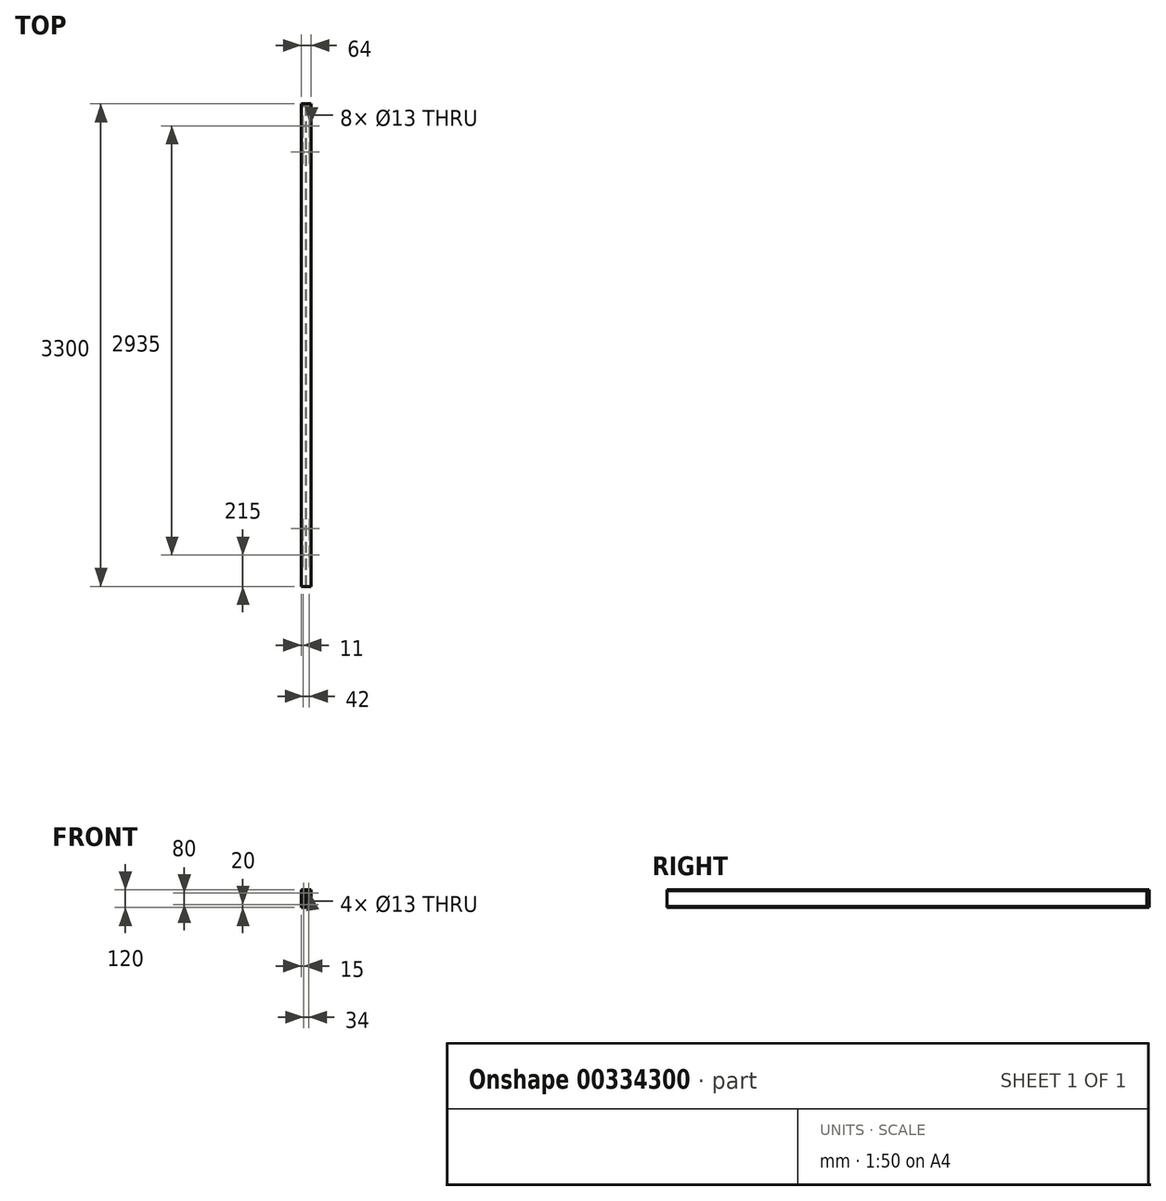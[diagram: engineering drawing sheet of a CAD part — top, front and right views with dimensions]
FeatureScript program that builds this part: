
annotation { "Feature Type Name" : "Feature", "Feature Type Description" : "" }
export const myFeature = defineFeature(function(context is Context, id is Id, definition is map)
    precondition{}
    {
        {
            var Q0;
            Q0=qCreatedBy(makeId("Front.planeOp"),FACE);
            var sketch = newSketch(context, id + "F0", { "sketchPlane" : qUnion([Q0])});
            skLineSegment(sketch, "E0", {"start": v(-32, 0) * mm, "end": v(32, 0) * mm});
            skLineSegment(sketch, "E1", {"start": v(32, 0) * mm, "end": v(32, 6.3) * mm});
            skLineSegment(sketch, "E2", {"start": v(32, 6.3) * mm, "end": v(9.2, 6.3) * mm});
            skLineSegment(sketch, "E3", {"start": v(2.2, 13.3) * mm, "end": v(2.2, 106.7) * mm});
            skLineSegment(sketch, "E4", {"start": v(9.2, 113.7) * mm, "end": v(32, 113.7) * mm});
            skLineSegment(sketch, "E5", {"start": v(32, 113.7) * mm, "end": v(32, 120) * mm});
            skLineSegment(sketch, "E6", {"start": v(32, 120) * mm, "end": v(-32, 120) * mm});
            skLineSegment(sketch, "E7", {"start": v(-32, 120) * mm, "end": v(-32, 113.7) * mm});
            skLineSegment(sketch, "E8", {"start": v(-32, 113.7) * mm, "end": v(-9.2, 113.7) * mm});
            skLineSegment(sketch, "E9", {"start": v(-2.2, 106.7) * mm, "end": v(-2.2, 13.3) * mm});
            skLineSegment(sketch, "E10", {"start": v(-9.2, 6.3) * mm, "end": v(-32, 6.3) * mm});
            skLineSegment(sketch, "E11", {"start": v(-32, 6.3) * mm, "end": v(-32, 0) * mm});
            skLineSegment(sketch, "E12", {"start": v(0, 0) * mm, "end": v(0, 0) * mm});
            skPoint(sketch, "E13.visualSharp", {"position": v(-2.2, 113.7) * mm});
            skArc(sketch, "E13.filletArc", {"start": v(-2.2, 106.7) * mm, "mid": v(-4.25, 111.65) * mm, "end": v(-9.2, 113.7) * mm});
            skPoint(sketch, "E14.visualSharp", {"position": v(-2.2, 6.3) * mm});
            skArc(sketch, "E14.filletArc", {"start": v(-9.2, 6.3) * mm, "mid": v(-4.25, 8.35) * mm, "end": v(-2.2, 13.3) * mm});
            skPoint(sketch, "E15.visualSharp", {"position": v(2.2, 6.3) * mm});
            skArc(sketch, "E15.filletArc", {"start": v(2.2, 13.3) * mm, "mid": v(4.25, 8.35) * mm, "end": v(9.2, 6.3) * mm});
            skPoint(sketch, "E16.visualSharp", {"position": v(2.2, 113.7) * mm});
            skArc(sketch, "E16.filletArc", {"start": v(9.2, 113.7) * mm, "mid": v(4.25, 111.65) * mm, "end": v(2.2, 106.7) * mm});
            skSolve(sketch);
        }
        {
            var Q0;
            Q0=makeQuery(id+"F0.imprint","IMPRINT",FACE,{"disambiguationData":[TD([[makeQuery(id+"F0.imprint","IMPRINT",EDGE,{"derivedFrom":sQuery(id+"F0.wireOp",EDGE,"E0")}),1.0]])]});
            extrude(context, id + "F1", {"entities" : qUnion([Q0]), "depth" : 300 * mm, "hasSecondDirection" : true, "secondDirectionOppositeDirection" : true, "secondDirectionDepth" : 3000 * mm});
        }
        {
            var Q0;
            Q0=makeQuery(id+"F1.opExtrude","CAP_FACE",FACE,{"disambiguationData":[OSD([sQuery(id+"F0.wireOp",EDGE,"E0"),sQuery(id+"F0.wireOp",EDGE,"E1"),sQuery(id+"F0.wireOp",EDGE,"E2"),sQuery(id+"F0.wireOp",EDGE,"E3"),sQuery(id+"F0.wireOp",EDGE,"E4"),sQuery(id+"F0.wireOp",EDGE,"E5"),sQuery(id+"F0.wireOp",EDGE,"E6"),sQuery(id+"F0.wireOp",EDGE,"E7"),sQuery(id+"F0.wireOp",EDGE,"E8"),sQuery(id+"F0.wireOp",EDGE,"E9"),sQuery(id+"F0.wireOp",EDGE,"E10"),sQuery(id+"F0.wireOp",EDGE,"E11"),sQuery(id+"F0.wireOp",EDGE,"E13.filletArc"),sQuery(id+"F0.wireOp",EDGE,"E14.filletArc"),sQuery(id+"F0.wireOp",EDGE,"E15.filletArc"),sQuery(id+"F0.wireOp",EDGE,"E16.filletArc")])],"isStart":true});
            var sketch = newSketch(context, id + "F2", { "sketchPlane" : qUnion([Q0])});
            skLineSegment(sketch, "E17.bottom", {"start": v(-32, 0) * mm, "end": v(32, 0) * mm});
            skLineSegment(sketch, "E17.top", {"start": v(-32, 120) * mm, "end": v(32, 120) * mm});
            skLineSegment(sketch, "E17.left", {"start": v(-32, 0) * mm, "end": v(-32, 120) * mm});
            skLineSegment(sketch, "E17.right", {"start": v(32, 0) * mm, "end": v(32, 120) * mm});
            skCircle(sketch, "E18", {"center": v(-17, 100) * mm, "radius": 6.5 * mm});
            skCircle(sketch, "E19", {"center": v(17, 100) * mm, "radius": 6.5 * mm});
            skCircle(sketch, "E20", {"center": v(17, 20) * mm, "radius": 6.5 * mm});
            skCircle(sketch, "E21", {"center": v(-17, 20) * mm, "radius": 6.5 * mm});
            skLineSegment(sketch, "E22", {"start": v(-17, 100) * mm, "end": v(17, 100) * mm, "construction": true});
            skLineSegment(sketch, "E23", {"start": v(-17, 20) * mm, "end": v(17, 20) * mm, "construction": true});
            skLineSegment(sketch, "E24", {"start": v(0, 120) * mm, "end": v(0, 0) * mm, "construction": true});
            skPoint(sketch, "E24.startSnap0", {"position": v(0, 120) * mm});
            skLineSegment(sketch, "E25", {"start": v(-32, 60) * mm, "end": v(32, 60) * mm, "construction": true});
            skSolve(sketch);
        }
        {
            var Q0;
            Q0=makeQuery(id+"F2.imprint","IMPRINT",FACE,{"disambiguationData":[TD([[makeQuery(id+"F2.imprint","IMPRINT",EDGE,{"derivedFrom":sQuery(id+"F2.wireOp",EDGE,"E19")}),-1.0]])]});
            var Q1;
            Q1=makeQuery(id+"F2.imprint","IMPRINT",FACE,{"disambiguationData":[TD([[makeQuery(id+"F2.imprint","IMPRINT",EDGE,{"derivedFrom":sQuery(id+"F2.wireOp",EDGE,"E18")}),-1.0]])]});
            var Q2;
            {var subQ3=sQuery(id+"F2.wireOp",EDGE,"E17.bottom");Q2=makeQuery(id+"F2.imprint","IMPRINT",FACE,{"disambiguationData":[TD([[makeQuery(id+"F2.imprint","IMPRINT",EDGE,{"derivedFrom":subQ3}),-1.0]])]});}
            extrude(context, id + "F3", {"entities" : qUnion([Q0, Q1, Q2]), "operationType" : NewBodyOperationType.ADD, "oppositeDirection" : true, "depth" : 12 * mm});
        }
        {
            var Q0;
            Q0=makeQuery(id+"F3.boolean.opBoolean","INTERSECT",EDGE,{"derivedFrom":[makeQuery(id+"F1.opExtrude","SWEPT_FACE",FACE,{"disambiguationData":[OSD([sQuery(id+"F0.wireOp",EDGE,"E4")])]}),makeQuery(id+"F3.opExtrude","CAP_FACE",FACE,{"disambiguationData":[OSD([sQuery(id+"F2.wireOp",EDGE,"E17.bottom"),sQuery(id+"F2.wireOp",EDGE,"E17.top"),sQuery(id+"F2.wireOp",EDGE,"E17.left"),sQuery(id+"F2.wireOp",EDGE,"E17.right"),sQuery(id+"F2.wireOp",EDGE,"E18"),sQuery(id+"F2.wireOp",EDGE,"E19"),sQuery(id+"F2.wireOp",EDGE,"E20"),sQuery(id+"F2.wireOp",EDGE,"E21")])],"isStart":false})]});
            var Q1;
            Q1=makeQuery(id+"F3.boolean.opBoolean","INTERSECT",EDGE,{"derivedFrom":[makeQuery(id+"F1.opExtrude","SWEPT_FACE",FACE,{"disambiguationData":[OSD([sQuery(id+"F0.wireOp",EDGE,"E16.filletArc")])]}),makeQuery(id+"F3.opExtrude","CAP_FACE",FACE,{"disambiguationData":[OSD([sQuery(id+"F2.wireOp",EDGE,"E17.bottom"),sQuery(id+"F2.wireOp",EDGE,"E17.top"),sQuery(id+"F2.wireOp",EDGE,"E17.left"),sQuery(id+"F2.wireOp",EDGE,"E17.right"),sQuery(id+"F2.wireOp",EDGE,"E18"),sQuery(id+"F2.wireOp",EDGE,"E19"),sQuery(id+"F2.wireOp",EDGE,"E20"),sQuery(id+"F2.wireOp",EDGE,"E21")])],"isStart":false})]});
            var Q2;
            Q2=makeQuery(id+"F3.boolean.opBoolean","INTERSECT",EDGE,{"derivedFrom":[makeQuery(id+"F1.opExtrude","SWEPT_FACE",FACE,{"disambiguationData":[OSD([sQuery(id+"F0.wireOp",EDGE,"E3")])]}),makeQuery(id+"F3.opExtrude","CAP_FACE",FACE,{"disambiguationData":[OSD([sQuery(id+"F2.wireOp",EDGE,"E17.bottom"),sQuery(id+"F2.wireOp",EDGE,"E17.top"),sQuery(id+"F2.wireOp",EDGE,"E17.left"),sQuery(id+"F2.wireOp",EDGE,"E17.right"),sQuery(id+"F2.wireOp",EDGE,"E18"),sQuery(id+"F2.wireOp",EDGE,"E19"),sQuery(id+"F2.wireOp",EDGE,"E20"),sQuery(id+"F2.wireOp",EDGE,"E21")])],"isStart":false})]});
            var Q3;
            Q3=makeQuery(id+"F3.boolean.opBoolean","INTERSECT",EDGE,{"derivedFrom":[makeQuery(id+"F1.opExtrude","SWEPT_FACE",FACE,{"disambiguationData":[OSD([sQuery(id+"F0.wireOp",EDGE,"E15.filletArc")])]}),makeQuery(id+"F3.opExtrude","CAP_FACE",FACE,{"disambiguationData":[OSD([sQuery(id+"F2.wireOp",EDGE,"E17.bottom"),sQuery(id+"F2.wireOp",EDGE,"E17.top"),sQuery(id+"F2.wireOp",EDGE,"E17.left"),sQuery(id+"F2.wireOp",EDGE,"E17.right"),sQuery(id+"F2.wireOp",EDGE,"E18"),sQuery(id+"F2.wireOp",EDGE,"E19"),sQuery(id+"F2.wireOp",EDGE,"E20"),sQuery(id+"F2.wireOp",EDGE,"E21")])],"isStart":false})]});
            var Q4;
            Q4=makeQuery(id+"F3.boolean.opBoolean","INTERSECT",EDGE,{"derivedFrom":[makeQuery(id+"F1.opExtrude","SWEPT_FACE",FACE,{"disambiguationData":[OSD([sQuery(id+"F0.wireOp",EDGE,"E2")])]}),makeQuery(id+"F3.opExtrude","CAP_FACE",FACE,{"disambiguationData":[OSD([sQuery(id+"F2.wireOp",EDGE,"E17.bottom"),sQuery(id+"F2.wireOp",EDGE,"E17.top"),sQuery(id+"F2.wireOp",EDGE,"E17.left"),sQuery(id+"F2.wireOp",EDGE,"E17.right"),sQuery(id+"F2.wireOp",EDGE,"E18"),sQuery(id+"F2.wireOp",EDGE,"E19"),sQuery(id+"F2.wireOp",EDGE,"E20"),sQuery(id+"F2.wireOp",EDGE,"E21")])],"isStart":false})]});
            chamfer(context, id + "F4", {"entities" : qUnion([Q0, Q1, Q2, Q3, Q4]), "width" : 3 * mm, "tangentPropagation" : true});
        }
        {
            var Q0;
            Q0=makeQuery(id+"F3.boolean.opBoolean","INTERSECT",EDGE,{"derivedFrom":[makeQuery(id+"F1.opExtrude","SWEPT_FACE",FACE,{"disambiguationData":[OSD([sQuery(id+"F0.wireOp",EDGE,"E10")])]}),makeQuery(id+"F3.opExtrude","CAP_FACE",FACE,{"disambiguationData":[OSD([sQuery(id+"F2.wireOp",EDGE,"E17.bottom"),sQuery(id+"F2.wireOp",EDGE,"E17.top"),sQuery(id+"F2.wireOp",EDGE,"E17.left"),sQuery(id+"F2.wireOp",EDGE,"E17.right"),sQuery(id+"F2.wireOp",EDGE,"E18"),sQuery(id+"F2.wireOp",EDGE,"E19"),sQuery(id+"F2.wireOp",EDGE,"E20"),sQuery(id+"F2.wireOp",EDGE,"E21")])],"isStart":false})]});
            var Q1;
            Q1=makeQuery(id+"F3.boolean.opBoolean","INTERSECT",EDGE,{"derivedFrom":[makeQuery(id+"F1.opExtrude","SWEPT_FACE",FACE,{"disambiguationData":[OSD([sQuery(id+"F0.wireOp",EDGE,"E14.filletArc")])]}),makeQuery(id+"F3.opExtrude","CAP_FACE",FACE,{"disambiguationData":[OSD([sQuery(id+"F2.wireOp",EDGE,"E17.bottom"),sQuery(id+"F2.wireOp",EDGE,"E17.top"),sQuery(id+"F2.wireOp",EDGE,"E17.left"),sQuery(id+"F2.wireOp",EDGE,"E17.right"),sQuery(id+"F2.wireOp",EDGE,"E18"),sQuery(id+"F2.wireOp",EDGE,"E19"),sQuery(id+"F2.wireOp",EDGE,"E20"),sQuery(id+"F2.wireOp",EDGE,"E21")])],"isStart":false})]});
            var Q2;
            Q2=makeQuery(id+"F3.boolean.opBoolean","INTERSECT",EDGE,{"derivedFrom":[makeQuery(id+"F1.opExtrude","SWEPT_FACE",FACE,{"disambiguationData":[OSD([sQuery(id+"F0.wireOp",EDGE,"E9")])]}),makeQuery(id+"F3.opExtrude","CAP_FACE",FACE,{"disambiguationData":[OSD([sQuery(id+"F2.wireOp",EDGE,"E17.bottom"),sQuery(id+"F2.wireOp",EDGE,"E17.top"),sQuery(id+"F2.wireOp",EDGE,"E17.left"),sQuery(id+"F2.wireOp",EDGE,"E17.right"),sQuery(id+"F2.wireOp",EDGE,"E18"),sQuery(id+"F2.wireOp",EDGE,"E19"),sQuery(id+"F2.wireOp",EDGE,"E20"),sQuery(id+"F2.wireOp",EDGE,"E21")])],"isStart":false})]});
            var Q3;
            Q3=makeQuery(id+"F3.boolean.opBoolean","INTERSECT",EDGE,{"derivedFrom":[makeQuery(id+"F1.opExtrude","SWEPT_FACE",FACE,{"disambiguationData":[OSD([sQuery(id+"F0.wireOp",EDGE,"E13.filletArc")])]}),makeQuery(id+"F3.opExtrude","CAP_FACE",FACE,{"disambiguationData":[OSD([sQuery(id+"F2.wireOp",EDGE,"E17.bottom"),sQuery(id+"F2.wireOp",EDGE,"E17.top"),sQuery(id+"F2.wireOp",EDGE,"E17.left"),sQuery(id+"F2.wireOp",EDGE,"E17.right"),sQuery(id+"F2.wireOp",EDGE,"E18"),sQuery(id+"F2.wireOp",EDGE,"E19"),sQuery(id+"F2.wireOp",EDGE,"E20"),sQuery(id+"F2.wireOp",EDGE,"E21")])],"isStart":false})]});
            var Q4;
            Q4=makeQuery(id+"F3.boolean.opBoolean","INTERSECT",EDGE,{"derivedFrom":[makeQuery(id+"F1.opExtrude","SWEPT_FACE",FACE,{"disambiguationData":[OSD([sQuery(id+"F0.wireOp",EDGE,"E8")])]}),makeQuery(id+"F3.opExtrude","CAP_FACE",FACE,{"disambiguationData":[OSD([sQuery(id+"F2.wireOp",EDGE,"E17.bottom"),sQuery(id+"F2.wireOp",EDGE,"E17.top"),sQuery(id+"F2.wireOp",EDGE,"E17.left"),sQuery(id+"F2.wireOp",EDGE,"E17.right"),sQuery(id+"F2.wireOp",EDGE,"E18"),sQuery(id+"F2.wireOp",EDGE,"E19"),sQuery(id+"F2.wireOp",EDGE,"E20"),sQuery(id+"F2.wireOp",EDGE,"E21")])],"isStart":false})]});
            chamfer(context, id + "F5", {"entities" : qUnion([Q0, Q1, Q2, Q3, Q4]), "width" : 3 * mm, "tangentPropagation" : true});
        }
        {
            var Q0;
            Q0=makeQuery(id+"F1.opExtrude","SWEPT_FACE",FACE,{"disambiguationData":[OSD([sQuery(id+"F0.wireOp",EDGE,"E0")])]});
            var sketch = newSketch(context, id + "F6", { "sketchPlane" : qUnion([Q0])});
            skLineSegment(sketch, "E26.bottom", {"start": v(21, -95) * mm, "end": v(-21, -95) * mm, "construction": true});
            skLineSegment(sketch, "E26.top", {"start": v(21, 85) * mm, "end": v(-21, 85) * mm, "construction": true});
            skLineSegment(sketch, "E26.left", {"start": v(21, -95) * mm, "end": v(21, 85) * mm, "construction": true});
            skLineSegment(sketch, "E26.right", {"start": v(-21, -95) * mm, "end": v(-21, 85) * mm, "construction": true});
            skPoint(sketch, "E26.middle", {"position": v(0, -5) * mm});
            skCircle(sketch, "E27", {"center": v(21, 85) * mm, "radius": 6.5 * mm});
            skCircle(sketch, "E28", {"center": v(21, -95) * mm, "radius": 6.5 * mm});
            skCircle(sketch, "E29", {"center": v(-21, -95) * mm, "radius": 6.5 * mm});
            skCircle(sketch, "E30", {"center": v(-21, 85) * mm, "radius": 6.5 * mm});
            skLineSegment(sketch, "E31.bottom", {"start": v(21, -2850) * mm, "end": v(-21, -2850) * mm, "construction": true});
            skLineSegment(sketch, "E31.top", {"start": v(21, -2670) * mm, "end": v(-21, -2670) * mm, "construction": true});
            skLineSegment(sketch, "E31.left", {"start": v(21, -2850) * mm, "end": v(21, -2670) * mm, "construction": true});
            skLineSegment(sketch, "E31.right", {"start": v(-21, -2850) * mm, "end": v(-21, -2670) * mm, "construction": true});
            skPoint(sketch, "E31.middle", {"position": v(0, -2760) * mm});
            skPoint(sketch, "E31.middle.positionSnap0", {"position": v(0, -95) * mm});
            skPoint(sketch, "E31.centerSnap0", {"position": v(0, -95) * mm});
            skCircle(sketch, "E32", {"center": v(-21, -2670) * mm, "radius": 6.5 * mm});
            skCircle(sketch, "E33", {"center": v(21, -2670) * mm, "radius": 6.5 * mm});
            skCircle(sketch, "E34", {"center": v(-21, -2850) * mm, "radius": 6.5 * mm});
            skCircle(sketch, "E35", {"center": v(21, -2850) * mm, "radius": 6.5 * mm});
            skSolve(sketch);
        }
        {
            var Q0;
            Q0=makeQuery(id+"F6.imprint","IMPRINT",FACE,{"disambiguationData":[TD([[makeQuery(id+"F6.imprint","IMPRINT",EDGE,{"derivedFrom":sQuery(id+"F6.wireOp",EDGE,"JJcsFfbY-181H-b44I-lAzz-ahYGcjGX36jE")}),1.0]])]});
            var Q1;
            Q1=makeQuery(id+"F6.imprint","IMPRINT",FACE,{"disambiguationData":[TD([[makeQuery(id+"F6.imprint","IMPRINT",EDGE,{"derivedFrom":sQuery(id+"F6.wireOp",EDGE,"8X0YDoZR-MKSx-xxUy-kiRu-iMODx4XVsFsO")}),1.0]])]});
            var Q2;
            Q2=makeQuery(id+"F6.imprint","IMPRINT",FACE,{"disambiguationData":[TD([[makeQuery(id+"F6.imprint","IMPRINT",EDGE,{"derivedFrom":sQuery(id+"F6.wireOp",EDGE,"7u1V7NTp-PA7n-3RXo-sr4M-a3gBre18wiXg")}),1.0]])]});
            var Q3;
            Q3=makeQuery(id+"F6.imprint","IMPRINT",FACE,{"disambiguationData":[TD([[makeQuery(id+"F6.imprint","IMPRINT",EDGE,{"derivedFrom":sQuery(id+"F6.wireOp",EDGE,"P3kTRWrh-zypR-1Pc7-TaIP-jTxsZJOuPHQd")}),1.0]])]});
            var Q4;
            Q4=makeQuery(id+"F6.imprint","IMPRINT",FACE,{"disambiguationData":[TD([[makeQuery(id+"F6.imprint","IMPRINT",EDGE,{"derivedFrom":sQuery(id+"F6.wireOp",EDGE,"dIOHaGGm-riHm-lTID-DCxn-ymXNWbhd4pZG")}),1.0]])]});
            var Q5;
            Q5=makeQuery(id+"F6.imprint","IMPRINT",FACE,{"disambiguationData":[TD([[makeQuery(id+"F6.imprint","IMPRINT",EDGE,{"derivedFrom":sQuery(id+"F6.wireOp",EDGE,"vp5bpoyW-BOQE-W55p-YgiJ-HtZX2Kjx4qEI")}),1.0]])]});
            var Q6;
            Q6=makeQuery(id+"F6.imprint","IMPRINT",FACE,{"disambiguationData":[TD([[makeQuery(id+"F6.imprint","IMPRINT",EDGE,{"derivedFrom":sQuery(id+"F6.wireOp",EDGE,"yILJJugs-jyyq-eTye-5h8z-FDoijVoQVvbv")}),1.0]])]});
            var Q7;
            Q7=makeQuery(id+"F6.imprint","IMPRINT",FACE,{"disambiguationData":[TD([[makeQuery(id+"F6.imprint","IMPRINT",EDGE,{"derivedFrom":sQuery(id+"F6.wireOp",EDGE,"QoqENZRi-UZpU-HqW0-CNnS-FCZrDTomPy0M")}),1.0]])]});
            var Q8;
            Q8=makeQuery(id+"F6.imprint","IMPRINT",FACE,{"disambiguationData":[TD([[makeQuery(id+"F6.imprint","IMPRINT",EDGE,{"derivedFrom":sQuery(id+"F6.wireOp",EDGE,"E27")}),1.0]])]});
            var Q9;
            Q9=makeQuery(id+"F6.imprint","IMPRINT",FACE,{"disambiguationData":[TD([[makeQuery(id+"F6.imprint","IMPRINT",EDGE,{"derivedFrom":sQuery(id+"F6.wireOp",EDGE,"E30")}),1.0]])]});
            var Q10;
            Q10=makeQuery(id+"F6.imprint","IMPRINT",FACE,{"disambiguationData":[TD([[makeQuery(id+"F6.imprint","IMPRINT",EDGE,{"derivedFrom":sQuery(id+"F6.wireOp",EDGE,"E29")}),1.0]])]});
            var Q11;
            Q11=makeQuery(id+"F6.imprint","IMPRINT",FACE,{"disambiguationData":[TD([[makeQuery(id+"F6.imprint","IMPRINT",EDGE,{"derivedFrom":sQuery(id+"F6.wireOp",EDGE,"E28")}),1.0]])]});
            var Q12;
            Q12=makeQuery(id+"F6.imprint","IMPRINT",FACE,{"disambiguationData":[TD([[makeQuery(id+"F6.imprint","IMPRINT",EDGE,{"derivedFrom":sQuery(id+"F6.wireOp",EDGE,"E32")}),1.0]])]});
            var Q13;
            Q13=makeQuery(id+"F6.imprint","IMPRINT",FACE,{"disambiguationData":[TD([[makeQuery(id+"F6.imprint","IMPRINT",EDGE,{"derivedFrom":sQuery(id+"F6.wireOp",EDGE,"E33")}),1.0]])]});
            var Q14;
            Q14=makeQuery(id+"F6.imprint","IMPRINT",FACE,{"disambiguationData":[TD([[makeQuery(id+"F6.imprint","IMPRINT",EDGE,{"derivedFrom":sQuery(id+"F6.wireOp",EDGE,"E35")}),1.0]])]});
            var Q15;
            Q15=makeQuery(id+"F6.imprint","IMPRINT",FACE,{"disambiguationData":[TD([[makeQuery(id+"F6.imprint","IMPRINT",EDGE,{"derivedFrom":sQuery(id+"F6.wireOp",EDGE,"E34")}),1.0]])]});
            extrude(context, id + "F7", {"entities" : qUnion([Q0, Q1, Q2, Q3, Q4, Q5, Q6, Q7, Q8, Q9, Q10, Q11, Q12, Q13, Q14, Q15]), "operationType" : NewBodyOperationType.REMOVE, "endBound" : BoundingType.UP_TO_NEXT, "oppositeDirection" : true, "depth" : 25 * mm});
        }
    });
